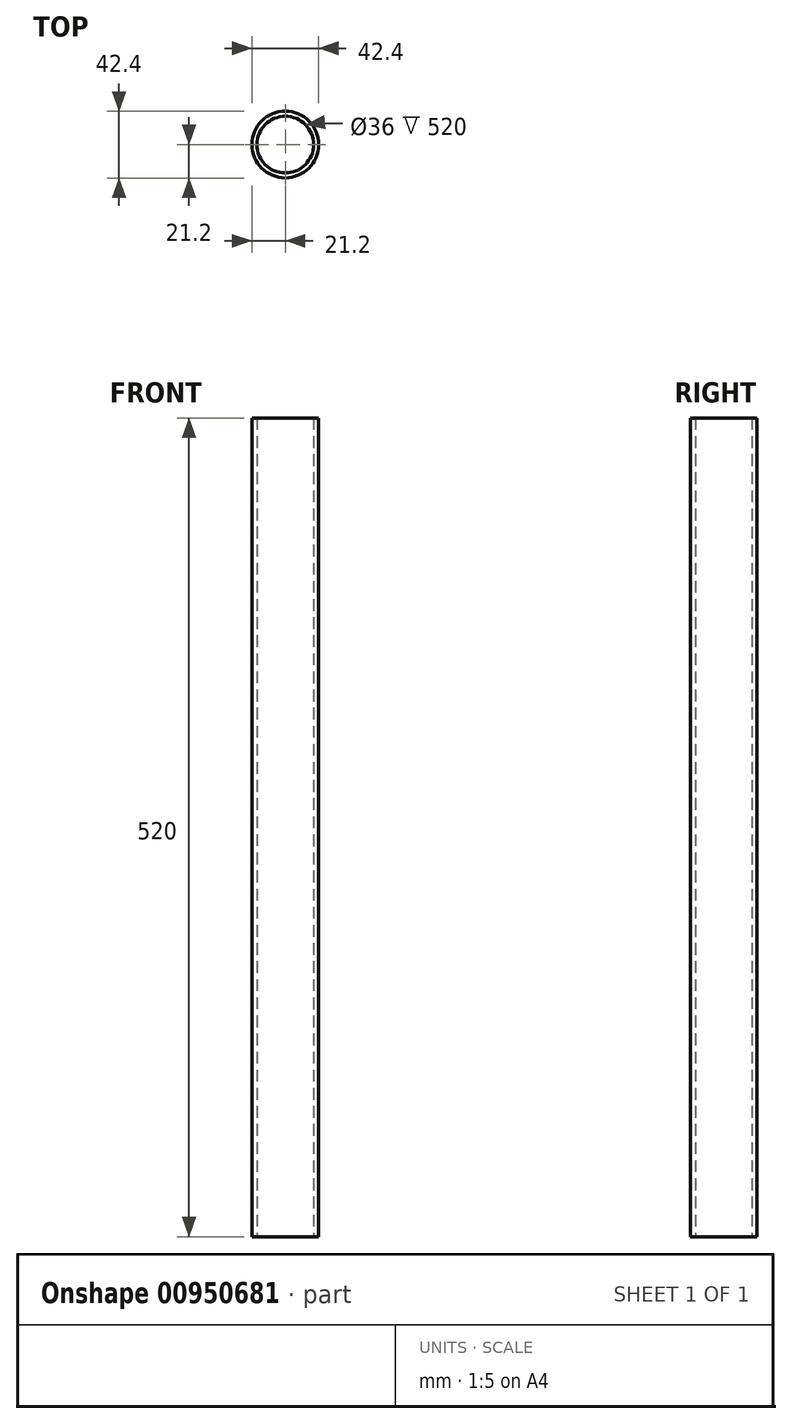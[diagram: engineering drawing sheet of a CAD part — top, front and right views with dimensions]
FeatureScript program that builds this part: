
annotation { "Feature Type Name" : "Feature", "Feature Type Description" : "" }
export const myFeature = defineFeature(function(context is Context, id is Id, definition is map)
    precondition{}
    {
        {
            var Q0;
            Q0=qCreatedBy(makeId("Top.planeOp"),FACE);
            var sketch = newSketch(context, id + "F0", { "sketchPlane" : qUnion([Q0])});
            skCircle(sketch, "E0", {"center": v(0, 0) * mm, "radius": 21.2 * mm});
            skCircle(sketch, "E1.0", {"center": v(0, 0) * mm, "radius": 18 * mm});
            skSolve(sketch);
        }
        {
            var Q0;
            Q0=makeQuery(id+"F0.imprint","IMPRINT",FACE,{"disambiguationData":[TD([[makeQuery(id+"F0.imprint","IMPRINT",EDGE,{"derivedFrom":sQuery(id+"F0.wireOp",EDGE,"E0")}),1.0]])]});
            extrude(context, id + "F1", {"entities" : qUnion([Q0]), "depth" : 520 * mm, "offsetDistance" : 25 * mm});
        }
    });
